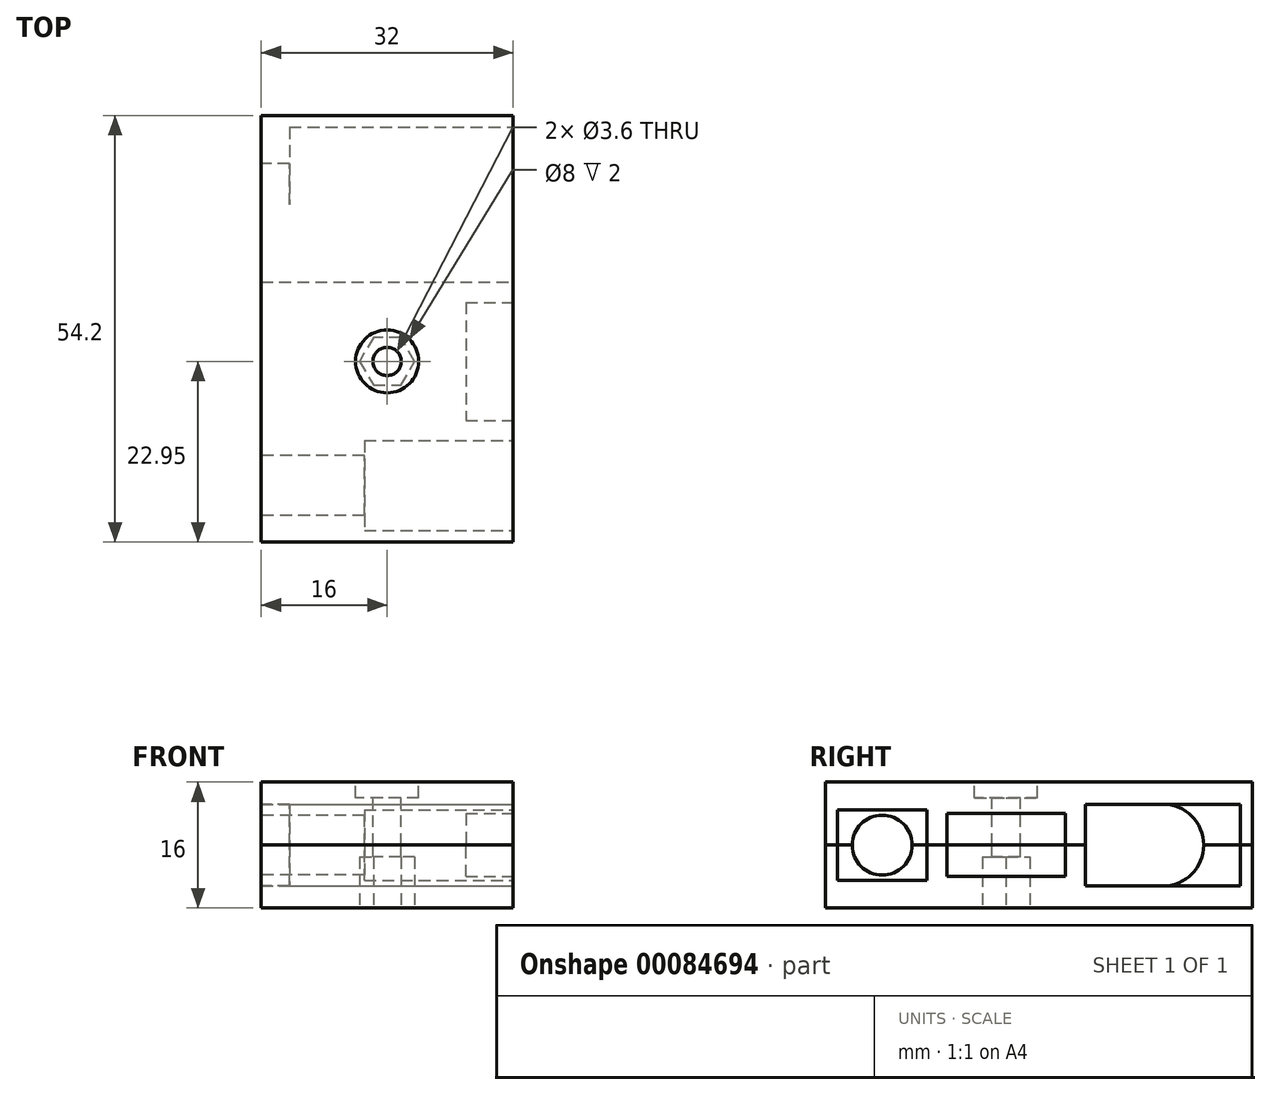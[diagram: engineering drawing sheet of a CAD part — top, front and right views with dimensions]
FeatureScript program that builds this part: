
annotation { "Feature Type Name" : "Feature", "Feature Type Description" : "" }
export const myFeature = defineFeature(function(context is Context, id is Id, definition is map)
    precondition{}
    {
        {
            var Q0;
            Q0=qCreatedBy(makeId("Right.planeOp"),FACE);
            var sketch = newSketch(context, id + "F0", { "sketchPlane" : qUnion([Q0])});
            skLineSegment(sketch, "E0", {"start": v(-27.1, 0) * mm, "end": v(-27.1, 8) * mm});
            skLineSegment(sketch, "E1", {"start": v(-27.1, 8) * mm, "end": v(27.1, 8) * mm});
            skLineSegment(sketch, "E2", {"start": v(27.1, 8) * mm, "end": v(27.1, 0) * mm});
            skPoint(sketch, "E3", {"position": v(0, 8) * mm});
            skLineSegment(sketch, "E4", {"start": v(27.1, 0) * mm, "end": v(-27.1, 0) * mm});
            skLineSegment(sketch, "E5", {"start": v(25.6, 0) * mm, "end": v(25.6, 5.2) * mm});
            skLineSegment(sketch, "E6", {"start": v(25.6, 5.2) * mm, "end": v(5.9, 5.2) * mm});
            skLineSegment(sketch, "E7", {"start": v(5.9, 5.2) * mm, "end": v(5.9, 0) * mm});
            skLineSegment(sketch, "E8", {"start": v(-14.2, 0) * mm, "end": v(-14.2, 4.5) * mm});
            skLineSegment(sketch, "E9", {"start": v(-14.2, 4.5) * mm, "end": v(-25.6, 4.5) * mm});
            skLineSegment(sketch, "E10", {"start": v(-25.6, 4.5) * mm, "end": v(-25.6, 0) * mm});
            skLineSegment(sketch, "E11", {"start": v(3.35, 0) * mm, "end": v(3.35, 4) * mm});
            skLineSegment(sketch, "E12", {"start": v(3.35, 4) * mm, "end": v(-11.65, 4) * mm});
            skLineSegment(sketch, "E13", {"start": v(-11.65, 4) * mm, "end": v(-11.65, 0) * mm});
            skLineSegment(sketch, "E14", {"start": v(5.9, 2.6) * mm, "end": v(3.35, 2.6) * mm, "construction": true});
            skLineSegment(sketch, "E15", {"start": v(-11.65, 2.25) * mm, "end": v(-14.2, 2.25) * mm, "construction": true});
            skSolve(sketch);
        }
        {
            var Q0;
            {var subQ3=sQuery(id+"F0.wireOp",EDGE,"E0");Q0=makeQuery(id+"F0.imprint","IMPRINT",FACE,{"disambiguationData":[TD([[makeQuery(id+"F0.imprint","IMPRINT",EDGE,{"derivedFrom":subQ3}),-1.0]])]});}
            extrude(context, id + "F1", {"entities" : qUnion([Q0]), "oppositeDirection" : true, "depth" : 32 * mm});
        }
        {
            var Q0;
            Q0=makeQuery(id+"F1.opExtrude","CAP_FACE",FACE,{"disambiguationData":[OSD([sQuery(id+"F0.wireOp",EDGE,"E0"),sQuery(id+"F0.wireOp",EDGE,"E1"),sQuery(id+"F0.wireOp",EDGE,"E2"),sQuery(id+"F0.wireOp",EDGE,"E4"),sQuery(id+"F0.wireOp",EDGE,"E5"),sQuery(id+"F0.wireOp",EDGE,"E6"),sQuery(id+"F0.wireOp",EDGE,"E7"),sQuery(id+"F0.wireOp",EDGE,"E8"),sQuery(id+"F0.wireOp",EDGE,"E9"),sQuery(id+"F0.wireOp",EDGE,"E10"),sQuery(id+"F0.wireOp",EDGE,"E11"),sQuery(id+"F0.wireOp",EDGE,"E12"),sQuery(id+"F0.wireOp",EDGE,"E13")])],"isStart":false});
            var sketch = newSketch(context, id + "F2", { "sketchPlane" : qUnion([Q0])});
            skLineSegment(sketch, "E16.0", {"start": v(-25.6, 0) * mm, "end": v(-25.6, 5.2) * mm});
            skLineSegment(sketch, "E17.0", {"start": v(-5.9, 5.2) * mm, "end": v(-5.9, 0) * mm});
            skLineSegment(sketch, "E18.bottom", {"start": v(-25.6, 0) * mm, "end": v(-5.9, 0) * mm});
            skLineSegment(sketch, "E18.top", {"start": v(-25.6, 5.2) * mm, "end": v(-5.9, 5.2) * mm});
            skLineSegment(sketch, "E18.right", {"start": v(-5.9, 0) * mm, "end": v(-5.9, 5.2) * mm});
            skArc(sketch, "E19", {"start": v(-10.55, 0) * mm, "mid": v(-15.75, 5.2) * mm, "end": v(-20.95, 0) * mm});
            skPoint(sketch, "E20.0", {"position": v(14.2, 0) * mm});
            skPoint(sketch, "E21.0", {"position": v(25.6, 4.5) * mm});
            skLineSegment(sketch, "E22.bottom", {"start": v(14.2, 0) * mm, "end": v(25.6, 0) * mm});
            skLineSegment(sketch, "E22.top", {"start": v(14.2, 4.5) * mm, "end": v(25.6, 4.5) * mm});
            skLineSegment(sketch, "E22.left", {"start": v(14.2, 0) * mm, "end": v(14.2, 4.5) * mm});
            skLineSegment(sketch, "E22.right", {"start": v(25.6, 0) * mm, "end": v(25.6, 4.5) * mm});
            skArc(sketch, "E23", {"start": v(16.1, 0) * mm, "mid": v(19.9, 3.8) * mm, "end": v(23.7, 0) * mm});
            skPoint(sketch, "E24.0", {"position": v(-3.35, 0) * mm});
            skPoint(sketch, "E25.0", {"position": v(11.65, 4) * mm});
            skLineSegment(sketch, "E26.bottom", {"start": v(-3.35, 0) * mm, "end": v(11.65, 0) * mm});
            skLineSegment(sketch, "E26.top", {"start": v(-3.35, 4) * mm, "end": v(11.65, 4) * mm});
            skLineSegment(sketch, "E26.left", {"start": v(-3.35, 0) * mm, "end": v(-3.35, 4) * mm});
            skLineSegment(sketch, "E26.right", {"start": v(11.65, 0) * mm, "end": v(11.65, 4) * mm});
            skSolve(sketch);
        }
        {
            var Q0;
            {var subQ0=sQuery(id+"F2.wireOp",EDGE,"E18.right");Q0=makeQuery(id+"F2.imprint","IMPRINT",FACE,{"disambiguationData":[TD([[makeQuery(id+"F2.imprint","IMPRINT",EDGE,{"derivedFrom":subQ0}),-1.0]])]});}
            var Q1;
            {var subQ0=sQuery(id+"F2.wireOp",EDGE,"E16.0");Q1=makeQuery(id+"F2.imprint","IMPRINT",FACE,{"disambiguationData":[TD([[makeQuery(id+"F2.imprint","IMPRINT",EDGE,{"derivedFrom":subQ0}),-1.0]])]});}
            extrude(context, id + "F3", {"entities" : qUnion([Q0, Q1]), "operationType" : NewBodyOperationType.ADD, "oppositeDirection" : true, "depth" : 3.6 * mm});
        }
        {
            var Q0;
            Q0=makeQuery(id+"F2.imprint","IMPRINT",FACE,{"disambiguationData":[TD([[makeQuery(id+"F2.imprint","IMPRINT",EDGE,{"derivedFrom":sQuery(id+"F2.wireOp",EDGE,"E22.top")}),-1.0]])]});
            extrude(context, id + "F4", {"entities" : qUnion([Q0]), "operationType" : NewBodyOperationType.ADD, "oppositeDirection" : true, "depth" : 13.1 * mm});
        }
        {
            var Q0;
            Q0=makeQuery(id+"F2.imprint","IMPRINT",FACE,{"disambiguationData":[TD([[makeQuery(id+"F2.imprint","IMPRINT",EDGE,{"derivedFrom":sQuery(id+"F2.wireOp",EDGE,"E26.bottom")}),1.0]])]});
            extrude(context, id + "F5", {"entities" : qUnion([Q0]), "operationType" : NewBodyOperationType.ADD, "oppositeDirection" : true, "depth" : 26 * mm});
        }
        {
            var Q0;
            Q0=makeQuery(id+"F1.opExtrude","SWEPT_BODY",BODY,{"disambiguationData":[OSD([sQuery(id+"F0.wireOp",EDGE,"E0"),sQuery(id+"F0.wireOp",EDGE,"E1"),sQuery(id+"F0.wireOp",EDGE,"E2"),sQuery(id+"F0.wireOp",EDGE,"E4"),sQuery(id+"F0.wireOp",EDGE,"E5"),sQuery(id+"F0.wireOp",EDGE,"E6"),sQuery(id+"F0.wireOp",EDGE,"E7"),sQuery(id+"F0.wireOp",EDGE,"E8"),sQuery(id+"F0.wireOp",EDGE,"E9"),sQuery(id+"F0.wireOp",EDGE,"E10"),sQuery(id+"F0.wireOp",EDGE,"E11"),sQuery(id+"F0.wireOp",EDGE,"E12"),sQuery(id+"F0.wireOp",EDGE,"E13")])]});
            var Q1;
            Q1=qCreatedBy(makeId("Top.planeOp"),FACE);
            mirror(context, id + "F6", {"entities" : qUnion([Q0]), "mirrorPlane" : qUnion([Q1])});
        }
        {
            var Q0;
            Q0=makeQuery(id+"F1.opExtrude","SWEPT_FACE",FACE,{"disambiguationData":[OSD([sQuery(id+"F0.wireOp",EDGE,"E1")])]});
            var sketch = newSketch(context, id + "F7", { "sketchPlane" : qUnion([Q0])});
            skLineSegment(sketch, "E27.0.0", {"start": v(-6, -11.65) * mm, "end": v(-6, 3.35) * mm});
            skLineSegment(sketch, "E27.0.1", {"start": v(-6, 3.35) * mm, "end": v(0, 3.35) * mm});
            skLineSegment(sketch, "E27.0.2", {"start": v(0, 3.35) * mm, "end": v(0, -11.65) * mm});
            skLineSegment(sketch, "E27.0.3", {"start": v(0, -11.65) * mm, "end": v(-6, -11.65) * mm});
            skLineSegment(sketch, "E28", {"start": v(-16, -27.1) * mm, "end": v(-16, 27.78) * mm, "construction": true});
            skPoint(sketch, "E28.endSnap0", {"position": v(-16, 27.1) * mm});
            skPoint(sketch, "E29", {"position": v(-16, -4.15) * mm});
            skPoint(sketch, "E29.positionSnap0", {"position": v(-6, -4.15) * mm});
            skCircle(sketch, "E30", {"center": v(-16, -4.15) * mm, "radius": 1.8 * mm});
            skCircle(sketch, "E31", {"center": v(-16, -4.15) * mm, "radius": 4 * mm});
            skSolve(sketch);
        }
        {
            var Q0;
            Q0=makeQuery(id+"F7.imprint","IMPRINT",FACE,{"disambiguationData":[TD([[makeQuery(id+"F7.imprint","IMPRINT",EDGE,{"derivedFrom":sQuery(id+"F7.wireOp",EDGE,"E30")}),1.0]])]});
            var Q1;
            Q1=makeQuery(id+"F6.opPattern","COPY",FACE,{"derivedFrom":makeQuery(id+"F1.opExtrude","SWEPT_FACE",FACE,{"disambiguationData":[OSD([sQuery(id+"F0.wireOp",EDGE,"E1")])]}),"instanceName":"1"});
            extrude(context, id + "F8", {"entities" : qUnion([Q0]), "operationType" : NewBodyOperationType.REMOVE, "endBound" : BoundingType.UP_TO_SURFACE, "oppositeDirection" : true, "endBoundEntityFace" : qUnion([Q1]), "depth" : 25 * mm});
        }
        {
            var Q0;
            Q0=makeQuery(id+"F7.imprint","IMPRINT",FACE,{"disambiguationData":[TD([[makeQuery(id+"F7.imprint","IMPRINT",EDGE,{"derivedFrom":sQuery(id+"F7.wireOp",EDGE,"E30")}),-1.0]])]});
            extrude(context, id + "F9", {"entities" : qUnion([Q0]), "operationType" : NewBodyOperationType.REMOVE, "oppositeDirection" : true, "depth" : 2 * mm});
        }
        {
            var Q0;
            Q0=makeQuery(id+"F6.opPattern","COPY",FACE,{"derivedFrom":makeQuery(id+"F1.opExtrude","SWEPT_FACE",FACE,{"disambiguationData":[OSD([sQuery(id+"F0.wireOp",EDGE,"E1")])]}),"instanceName":"1"});
            var sketch = newSketch(context, id + "F10", { "sketchPlane" : qUnion([Q0])});
            skCircle(sketch, "E32.0", {"center": v(-16, 4.15) * mm, "radius": 1.8 * mm});
            skCircle(sketch, "E33.cCircle", {"center": v(-16, 4.15) * mm, "radius": 3.5 * mm, "construction": true});
            skLineSegment(sketch, "E33.0", {"start": v(-14.25, 1.12) * mm, "end": v(-17.75, 1.12) * mm});
            skLineSegment(sketch, "E33.1", {"start": v(-17.75, 1.12) * mm, "end": v(-19.5, 4.15) * mm});
            skLineSegment(sketch, "E33.2", {"start": v(-19.5, 4.15) * mm, "end": v(-17.75, 7.18) * mm});
            skLineSegment(sketch, "E33.3", {"start": v(-17.75, 7.18) * mm, "end": v(-14.25, 7.18) * mm});
            skLineSegment(sketch, "E33.4", {"start": v(-14.25, 7.18) * mm, "end": v(-12.5, 4.15) * mm});
            skLineSegment(sketch, "E33.5", {"start": v(-12.5, 4.15) * mm, "end": v(-14.25, 1.12) * mm});
            skSolve(sketch);
        }
        {
            var Q0;
            Q0=makeQuery(id+"F10.imprint","IMPRINT",FACE,{"disambiguationData":[TD([[makeQuery(id+"F10.imprint","IMPRINT",EDGE,{"derivedFrom":sQuery(id+"F10.wireOp",EDGE,"E32.0")}),-1.0]])]});
            extrude(context, id + "F11", {"entities" : qUnion([Q0]), "operationType" : NewBodyOperationType.REMOVE, "oppositeDirection" : true, "depth" : 6.5 * mm});
        }
    });
